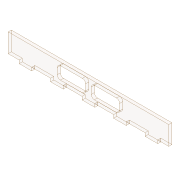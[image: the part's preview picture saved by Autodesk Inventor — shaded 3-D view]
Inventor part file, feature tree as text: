
AUTODESK INVENTOR PART (.ipt)
format: ipt  version: 2020 (Build 240168000, 168)  size: 152,064 bytes
history: native  units: in
note: dims shown in document units (in); Inventor stores cm internally (conversion verified against a paired STEP export)
features: extrude x3, sketch x3
ambient origin geometry x8: Origin, YZ Plane, XZ Plane, XY Plane, X Axis, Y Axis, Z Axis, Center Point
bodies: Solid1 (feature_tree)
feature tree (6):
  extrude  "Extrusion1"  Depth=1.1811in
  extrude  "Extrusion2"  Depth=0.7874in
  extrude  "Extrusion3"  Depth=0.689in
  sketch  "Sketch1"  dims[d0=10.0394in d1=1.1811in]
  sketch  "Sketch2"  dims[d2=0.1969in d3=0.0in d4=0.7874in]
  sketch  "Sketch3"  dims[d5=0.1969in d6=0.689in d7=1.9685in d9=1.9685in d10=0.3937in d12=0.3937in d14=0.689in d15=0.1969in d16=0.0in d17=1.7717in d18=0.7874in d19=1.063in d20=0.3937in d21=0.0in d22=0.1969in]
